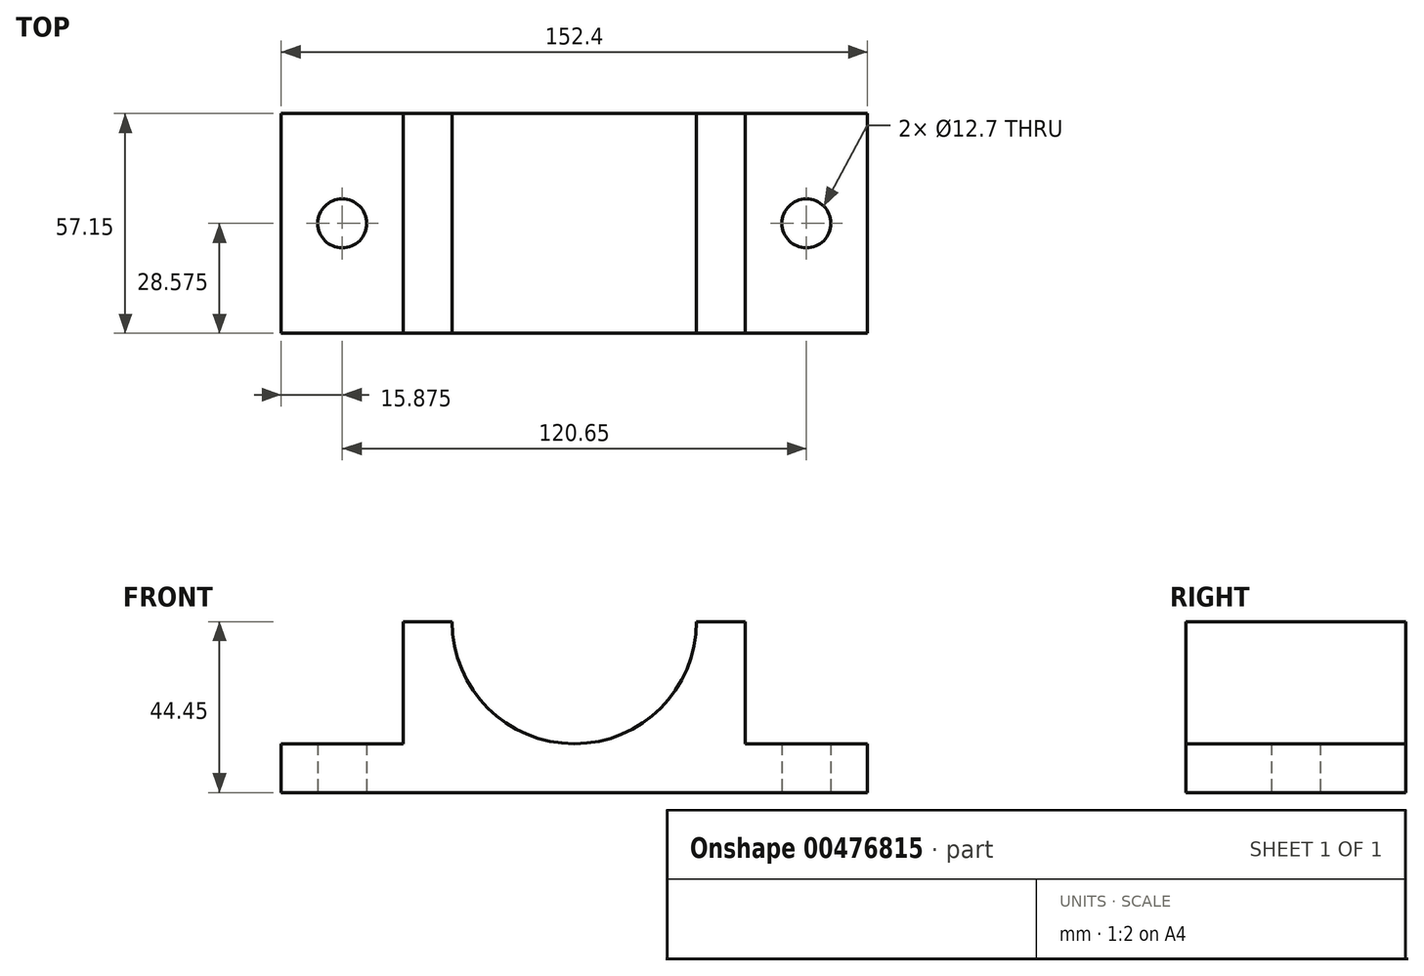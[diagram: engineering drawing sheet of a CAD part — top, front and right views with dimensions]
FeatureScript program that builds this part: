
annotation { "Feature Type Name" : "Feature", "Feature Type Description" : "" }
export const myFeature = defineFeature(function(context is Context, id is Id, definition is map)
    precondition{}
    {
        {
            var Q0;
            Q0=qCreatedBy(makeId("Top.planeOp"),FACE);
            var sketch = newSketch(context, id + "F0", { "sketchPlane" : qUnion([Q0])});
            skLineSegment(sketch, "E0.bottom", {"start": v(0, 0) * mm, "end": v(152.4, 0) * mm});
            skLineSegment(sketch, "E0.top", {"start": v(0, 57.15) * mm, "end": v(152.4, 57.15) * mm});
            skLineSegment(sketch, "E0.left", {"start": v(0, 0) * mm, "end": v(0, 57.15) * mm});
            skLineSegment(sketch, "E0.right", {"start": v(152.4, 0) * mm, "end": v(152.4, 57.15) * mm});
            skLineSegment(sketch, "E1", {"start": v(120.65, 57.15) * mm, "end": v(120.65, 0) * mm});
            skLineSegment(sketch, "E2", {"start": v(120.65, 57.15) * mm, "end": v(31.75, 57.15) * mm});
            skLineSegment(sketch, "E3", {"start": v(31.75, 57.15) * mm, "end": v(31.75, 0) * mm});
            skCircle(sketch, "E4", {"center": v(15.88, 28.57) * mm, "radius": 6.35 * mm});
            skCircle(sketch, "E5", {"center": v(136.53, 28.58) * mm, "radius": 6.35 * mm});
            skSolve(sketch);
        }
        {
            var Q0;
            {var subQ0=sQuery(id+"F0.wireOp",EDGE,"E0.right");Q0=makeQuery(id+"F0.imprint","IMPRINT",FACE,{"disambiguationData":[TD([[makeQuery(id+"F0.imprint","IMPRINT",EDGE,{"derivedFrom":subQ0}),1.0]])]});}
            var Q1;
            {var subQ1=sQuery(id+"F0.wireOp",EDGE,"E0.left");Q1=makeQuery(id+"F0.imprint","IMPRINT",FACE,{"disambiguationData":[TD([[makeQuery(id+"F0.imprint","IMPRINT",EDGE,{"derivedFrom":subQ1}),-1.0]])]});}
            var Q2;
            {var subQ0=sQuery(id+"F0.wireOp",EDGE,"E1");Q2=makeQuery(id+"F0.imprint","IMPRINT",FACE,{"disambiguationData":[TD([[makeQuery(id+"F0.imprint","IMPRINT",EDGE,{"derivedFrom":subQ0}),-1.0]])]});}
            extrude(context, id + "F1", {"entities" : qUnion([Q0, Q1, Q2]), "depth" : 12.7 * mm});
        }
        {
            var Q0;
            Q0=makeQuery(id+"F1.opExtrude","SWEPT_FACE",FACE,{"disambiguationData":[OSD([sQuery(id+"F0.wireOp",EDGE,"E0.bottom")])]});
            var sketch = newSketch(context, id + "F2", { "sketchPlane" : qUnion([Q0])});
            skLineSegment(sketch, "E6", {"start": v(76.2, 0) * mm, "end": v(76.2, 44.45) * mm});
            skPoint(sketch, "E6.endSnap0", {"position": v(76.2, 12.7) * mm});
            skArc(sketch, "E7", {"start": v(44.45, 44.45) * mm, "mid": v(76.2, 12.7) * mm, "end": v(107.95, 44.45) * mm});
            skLineSegment(sketch, "E8", {"start": v(44.45, 44.45) * mm, "end": v(31.75, 44.45) * mm});
            skLineSegment(sketch, "E9", {"start": v(31.75, 44.45) * mm, "end": v(31.75, 12.7) * mm});
            skLineSegment(sketch, "E10", {"start": v(31.75, 12.7) * mm, "end": v(120.65, 12.7) * mm});
            skLineSegment(sketch, "E11", {"start": v(120.65, 12.7) * mm, "end": v(120.65, 44.45) * mm});
            skLineSegment(sketch, "E12", {"start": v(120.65, 44.45) * mm, "end": v(107.95, 44.45) * mm});
            skSolve(sketch);
        }
        {
            var Q0;
            Q0=qSketchRegion(id+"F2",true);
            extrude(context, id + "F3", {"entities" : qUnion([Q0]), "operationType" : NewBodyOperationType.ADD, "oppositeDirection" : true, "depth" : 57.15 * mm});
        }
    });
